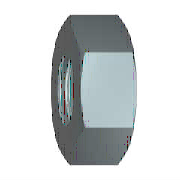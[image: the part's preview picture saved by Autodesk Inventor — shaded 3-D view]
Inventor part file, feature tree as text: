
AUTODESK INVENTOR PART (.ipt)
format: ipt  version: 2024.2 (Build 282272000, 272)  size: 172,032 bytes
history: native  units: mm (DEFAULTED — no unit token found)
features: chamfer x1, hole x1, other x1, plane x1
ambient origin geometry x7: Origin, YZ Plane, XZ Plane, X Axis, Y Axis, Z Axis, Center Point
bodies: Solid1 (feature_tree), Body (feature_tree)
feature tree (4):
  chamfer  "Chamfer1"  Distance=20.78461mm
  hole  "Thread"  [1 undecoded]
  other  "Work Axis1"
  plane  "Work Plane1"
note: 1 required parameter value undecoded (feature->parameter linkage not recoverable at this tier; creation-order binding heuristic only, values carry confidence <= 0.55)
